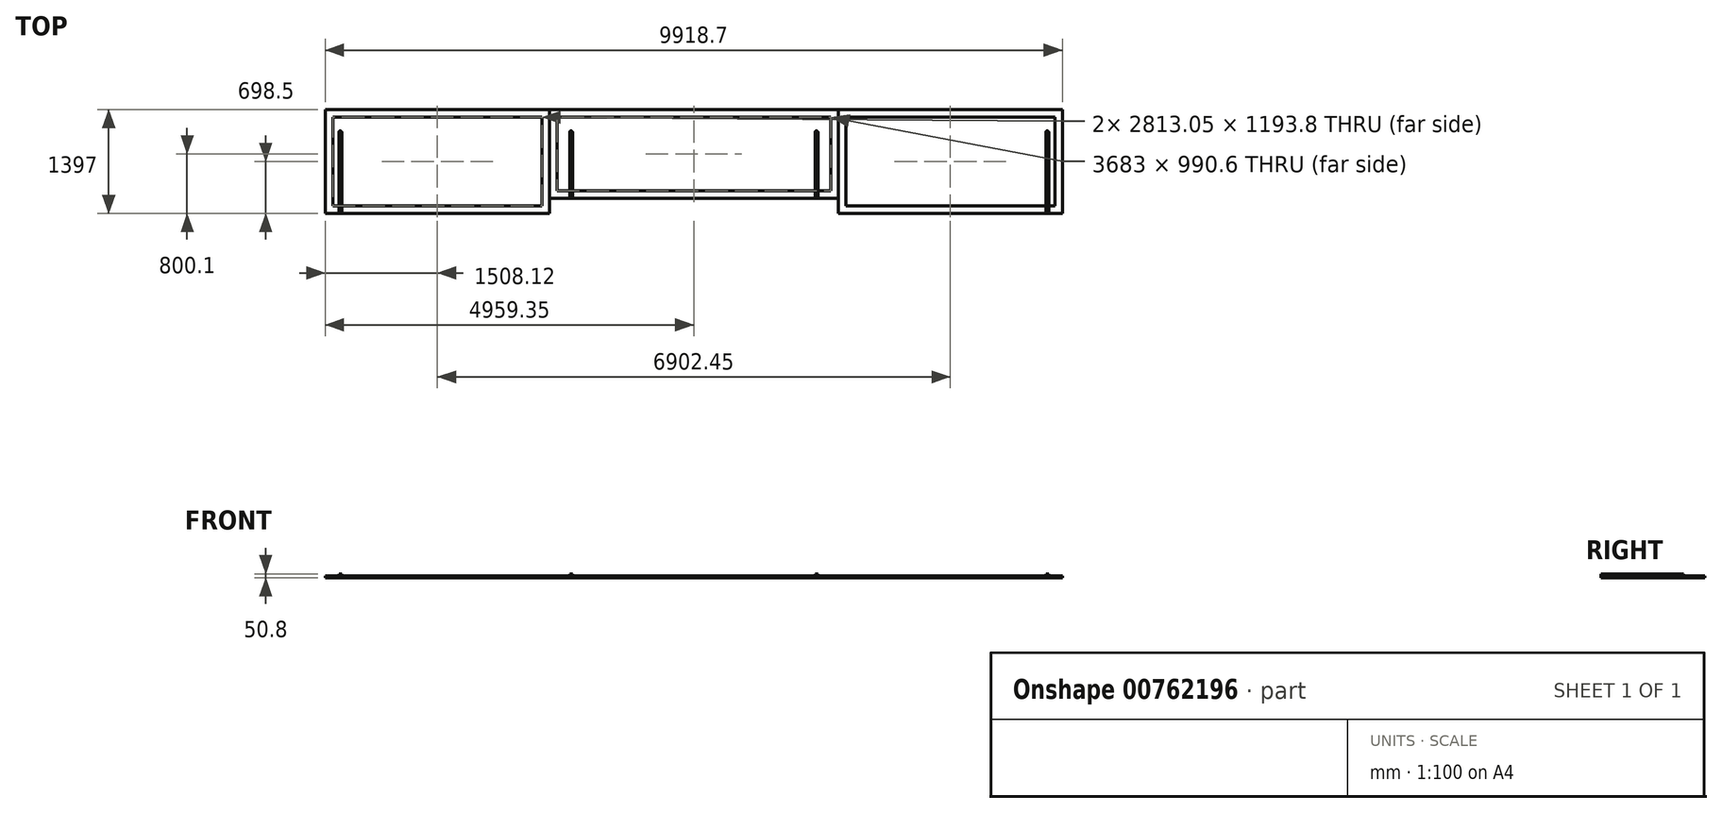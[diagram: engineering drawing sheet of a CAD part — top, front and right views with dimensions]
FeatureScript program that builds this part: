
annotation { "Feature Type Name" : "Feature", "Feature Type Description" : "" }
export const myFeature = defineFeature(function(context is Context, id is Id, definition is map)
    precondition{}
    {
        {
            var Q0;
            Q0=qCreatedBy(makeId("Top.planeOp"),FACE);
            var sketch = newSketch(context, id + "F0", { "sketchPlane" : qUnion([Q0])});
            skLineSegment(sketch, "E0", {"start": v(0, 0) * mm, "end": v(9918.7, 0) * mm});
            skLineSegment(sketch, "E1", {"start": v(9918.7, 0) * mm, "end": v(9918.7, -1397) * mm});
            skLineSegment(sketch, "E2", {"start": v(9918.7, -1397) * mm, "end": v(6902.45, -1397) * mm});
            skLineSegment(sketch, "E3", {"start": v(6902.45, -1397) * mm, "end": v(6902.45, -1193.8) * mm});
            skLineSegment(sketch, "E4", {"start": v(6902.45, -1193.8) * mm, "end": v(3016.25, -1193.8) * mm});
            skLineSegment(sketch, "E5", {"start": v(3016.25, -1193.8) * mm, "end": v(3016.25, -1397) * mm});
            skLineSegment(sketch, "E6", {"start": v(3016.25, -1397) * mm, "end": v(0, -1397) * mm});
            skLineSegment(sketch, "E7", {"start": v(0, -1397) * mm, "end": v(0, 0) * mm});
            skLineSegment(sketch, "E8.0", {"start": v(101.6, -1295.4) * mm, "end": v(101.6, -101.6) * mm});
            skLineSegment(sketch, "E8.1", {"start": v(2914.65, -1295.4) * mm, "end": v(101.6, -1295.4) * mm});
            skLineSegment(sketch, "E8.2", {"start": v(101.6, -101.6) * mm, "end": v(2914.65, -101.6) * mm});
            skLineSegment(sketch, "E8.3", {"start": v(2914.65, -1092.2) * mm, "end": v(2914.65, -1295.4) * mm});
            skLineSegment(sketch, "E8.4", {"start": v(9817.1, -101.6) * mm, "end": v(9817.1, -1295.4) * mm});
            skLineSegment(sketch, "E8.5", {"start": v(9817.1, -1295.4) * mm, "end": v(7004.05, -1295.4) * mm});
            skLineSegment(sketch, "E8.6", {"start": v(7004.05, -1295.4) * mm, "end": v(7004.05, -1092.2) * mm});
            skLineSegment(sketch, "E9", {"start": v(3016.25, -1193.8) * mm, "end": v(3016.25, 0) * mm});
            skLineSegment(sketch, "E10", {"start": v(6902.45, -1193.8) * mm, "end": v(6902.45, 0) * mm});
            skLineSegment(sketch, "E11", {"start": v(7004.05, -1092.2) * mm, "end": v(7004.05, -101.6) * mm});
            skLineSegment(sketch, "E12", {"start": v(2914.65, -1092.2) * mm, "end": v(2914.65, -101.6) * mm});
            skLineSegment(sketch, "E13", {"start": v(3117.85, -101.6) * mm, "end": v(3117.85, -1092.2) * mm});
            skLineSegment(sketch, "E14", {"start": v(6800.85, -101.6) * mm, "end": v(6800.85, -1092.2) * mm});
            skPoint(sketch, "E15.orphan", {"position": v(2914.65, 0) * mm});
            skLineSegment(sketch, "E16.trimOffspring", {"start": v(3117.85, -101.6) * mm, "end": v(6800.85, -101.6) * mm});
            skLineSegment(sketch, "E17.trimOffspring", {"start": v(7004.05, -101.6) * mm, "end": v(9817.1, -101.6) * mm});
            skLineSegment(sketch, "E18.trimOffspring", {"start": v(6800.85, -1092.2) * mm, "end": v(3117.85, -1092.2) * mm});
            skPoint(sketch, "E19.orphan", {"position": v(7004.05, 0) * mm});
            skSolve(sketch);
        }
        {
            var Q0;
            Q0=makeQuery(id+"F0.imprint","IMPRINT",FACE,{"disambiguationData":[TD([[makeQuery(id+"F0.imprint","IMPRINT",EDGE,{"derivedFrom":sQuery(id+"F0.wireOp",EDGE,"E5")}),-1.0]])]});
            extrude(context, id + "F1", {"entities" : qUnion([Q0]), "depth" : 25.4 * mm, "offsetDistance" : 25.4 * mm});
        }
        {
            var Q0;
            Q0=makeQuery(id+"F0.imprint","IMPRINT",FACE,{"disambiguationData":[TD([[makeQuery(id+"F0.imprint","IMPRINT",EDGE,{"derivedFrom":sQuery(id+"F0.wireOp",EDGE,"E4")}),-1.0]])]});
            extrude(context, id + "F2", {"entities" : qUnion([Q0]), "depth" : 25.4 * mm, "offsetDistance" : 25.4 * mm});
        }
        {
            var Q0;
            {var subQ0=sQuery(id+"F0.wireOp",EDGE,"E1");Q0=makeQuery(id+"F0.imprint","IMPRINT",FACE,{"disambiguationData":[TD([[makeQuery(id+"F0.imprint","IMPRINT",EDGE,{"derivedFrom":subQ0}),-1.0]])]});}
            extrude(context, id + "F3", {"entities" : qUnion([Q0]), "depth" : 25.4 * mm, "offsetDistance" : 25.4 * mm});
        }
        {
            var Q0;
            Q0=makeQuery(id+"F1.opExtrude","CAP_FACE",FACE,{"disambiguationData":[OSD([sQuery(id+"F0.wireOp",EDGE,"E0"),sQuery(id+"F0.wireOp",EDGE,"E1"),sQuery(id+"F0.wireOp",EDGE,"E2"),sQuery(id+"F0.wireOp",EDGE,"E3"),sQuery(id+"F0.wireOp",EDGE,"E4"),sQuery(id+"F0.wireOp",EDGE,"E5"),sQuery(id+"F0.wireOp",EDGE,"E6"),sQuery(id+"F0.wireOp",EDGE,"E7"),sQuery(id+"F0.wireOp",EDGE,"E8.0"),sQuery(id+"F0.wireOp",EDGE,"E8.1"),sQuery(id+"F0.wireOp",EDGE,"E8.2"),sQuery(id+"F0.wireOp",EDGE,"E8.3"),sQuery(id+"F0.wireOp",EDGE,"E8.4"),sQuery(id+"F0.wireOp",EDGE,"E8.5"),sQuery(id+"F0.wireOp",EDGE,"E8.6"),sQuery(id+"F0.wireOp",EDGE,"E8.7")])],"isStart":false});
            var sketch = newSketch(context, id + "F4", { "sketchPlane" : qUnion([Q0])});
            skLineSegment(sketch, "E20.bottom", {"start": v(184.15, -1397) * mm, "end": v(222.25, -1397) * mm});
            skLineSegment(sketch, "E20.top", {"start": v(184.15, -304.8) * mm, "end": v(222.25, -304.8) * mm});
            skLineSegment(sketch, "E20.left", {"start": v(184.15, -1397) * mm, "end": v(184.15, -304.8) * mm});
            skLineSegment(sketch, "E20.right", {"start": v(222.25, -1397) * mm, "end": v(222.25, -304.8) * mm});
            skLineSegment(sketch, "E21.bottom", {"start": v(3289.3, -1193.8) * mm, "end": v(3327.4, -1193.8) * mm});
            skLineSegment(sketch, "E21.top", {"start": v(3289.3, -304.8) * mm, "end": v(3327.4, -304.8) * mm});
            skLineSegment(sketch, "E21.left", {"start": v(3289.3, -1193.8) * mm, "end": v(3289.3, -304.8) * mm});
            skLineSegment(sketch, "E21.right", {"start": v(3327.4, -1193.8) * mm, "end": v(3327.4, -304.8) * mm});
            skLineSegment(sketch, "E22.bottom", {"start": v(6591.3, -1193.8) * mm, "end": v(6629.4, -1193.8) * mm});
            skLineSegment(sketch, "E22.top", {"start": v(6591.3, -304.8) * mm, "end": v(6629.4, -304.8) * mm});
            skLineSegment(sketch, "E22.left", {"start": v(6591.3, -1193.8) * mm, "end": v(6591.3, -304.8) * mm});
            skLineSegment(sketch, "E22.right", {"start": v(6629.4, -1193.8) * mm, "end": v(6629.4, -304.8) * mm});
            skLineSegment(sketch, "E23.bottom", {"start": v(9696.45, -1397) * mm, "end": v(9734.55, -1397) * mm});
            skLineSegment(sketch, "E23.top", {"start": v(9696.45, -304.8) * mm, "end": v(9734.55, -304.8) * mm});
            skLineSegment(sketch, "E23.left", {"start": v(9696.45, -1397) * mm, "end": v(9696.45, -304.8) * mm});
            skLineSegment(sketch, "E23.right", {"start": v(9734.55, -1397) * mm, "end": v(9734.55, -304.8) * mm});
            skCircle(sketch, "E24", {"center": v(203.2, -304.8) * mm, "radius": 19.05 * mm});
            skCircle(sketch, "E25", {"center": v(3308.35, -304.8) * mm, "radius": 19.05 * mm});
            skCircle(sketch, "E26", {"center": v(6610.35, -304.8) * mm, "radius": 19.05 * mm});
            skCircle(sketch, "E27", {"center": v(9715.5, -304.8) * mm, "radius": 19.05 * mm});
            skSolve(sketch);
        }
        {
            var Q0;
            Q0 = qSketchRegion(id + "F4", true);
            extrude(context, id + "F5", {"entities" : qUnion([Q0]), "depth" : 25.4 * mm, "offsetDistance" : 25.4 * mm});
        }
    });
